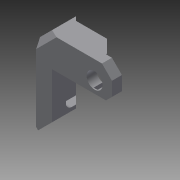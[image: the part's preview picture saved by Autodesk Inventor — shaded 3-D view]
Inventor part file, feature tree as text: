
AUTODESK INVENTOR PART (.ipt)
format: ipt  version: 2015 (Build 190159000, 159)  size: 132,608 bytes
history: native  units: mm
features: sketch x8, other x3
ambient origin geometry x8: Origin, YZ Plane, XZ Plane, XY Plane, X Axis, Y Axis, Z Axis, Center Point
bodies: Solid1 (feature_tree)
feature tree (11):
  other  "z-axis-top.ipt"
  other  "Solid1::z-axis-top.ipt"
  other  "TaggingFeature1"
  sketch  "Sketch1"  dims[d0=10.0mm]
  sketch  "Sketch2"
  sketch  "Sketch3"
  sketch  "Sketch4"
  sketch  "Sketch5"
  sketch  "Sketch6"
  sketch  "Sketch7"
  sketch  "Sketch8"
